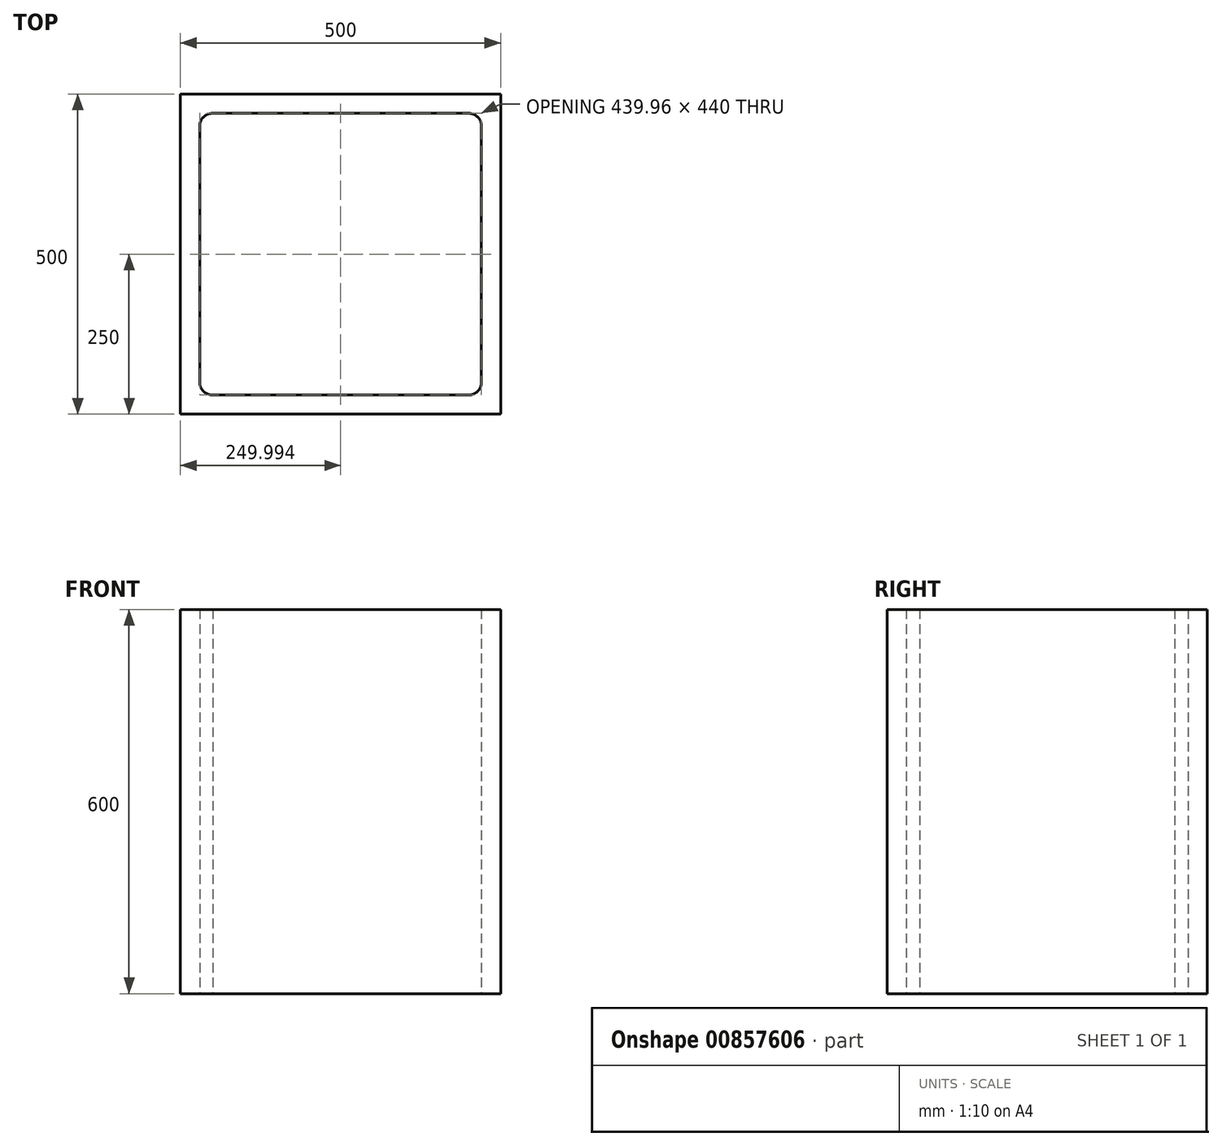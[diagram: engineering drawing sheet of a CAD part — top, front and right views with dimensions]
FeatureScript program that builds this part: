
annotation { "Feature Type Name" : "Feature", "Feature Type Description" : "" }
export const myFeature = defineFeature(function(context is Context, id is Id, definition is map)
    precondition{}
    {
        {
            var Q0;
            Q0=qCreatedBy(makeId("Top.planeOp"),FACE);
            var sketch = newSketch(context, id + "F0", { "sketchPlane" : qUnion([Q0])});
            skLineSegment(sketch, "E0.bottom", {"start": v(250, 250) * mm, "end": v(-250, 250) * mm});
            skLineSegment(sketch, "E0.top", {"start": v(250, -250) * mm, "end": v(-250, -250) * mm});
            skLineSegment(sketch, "E0.left", {"start": v(250, 250) * mm, "end": v(250, -250) * mm});
            skLineSegment(sketch, "E0.right", {"start": v(-250, 250) * mm, "end": v(-250, -250) * mm});
            skPoint(sketch, "E0.middle", {"position": v(0, 0) * mm});
            skLineSegment(sketch, "E1.bottom", {"start": v(200, 200) * mm, "end": v(-200, 200) * mm, "construction": true});
            skLineSegment(sketch, "E1.top", {"start": v(200, -200) * mm, "end": v(-200, -200) * mm, "construction": true});
            skLineSegment(sketch, "E1.left", {"start": v(200, 200) * mm, "end": v(200, -200) * mm, "construction": true});
            skLineSegment(sketch, "E1.right", {"start": v(-200, 200) * mm, "end": v(-200, -200) * mm, "construction": true});
            skArc(sketch, "E2", {"start": v(-199.85, 220) * mm, "mid": v(-214.34, 213.94) * mm, "end": v(-219.99, 199.3) * mm});
            skArc(sketch, "E3", {"start": v(219.98, 199.03) * mm, "mid": v(214.48, 213.8) * mm, "end": v(200, 220) * mm});
            skArc(sketch, "E4", {"start": v(200, -220) * mm, "mid": v(214.48, -213.8) * mm, "end": v(219.98, -199.03) * mm});
            skArc(sketch, "E5", {"start": v(-219.99, -199.3) * mm, "mid": v(-214.27, -214) * mm, "end": v(-199.67, -220) * mm});
            skLineSegment(sketch, "E6", {"start": v(-200.15, 220) * mm, "end": v(200, 220) * mm});
            skLineSegment(sketch, "E7", {"start": v(-219.99, 200.7) * mm, "end": v(-219.99, -200.7) * mm});
            skLineSegment(sketch, "E8", {"start": v(-200.33, -220) * mm, "end": v(200, -220) * mm});
            skLineSegment(sketch, "E9", {"start": v(219.98, -199.03) * mm, "end": v(219.98, 200) * mm});
            skSolve(sketch);
        }
        {
            var Q0;
            Q0 = qSketchRegion(id + "F0", true);
            extrude(context, id + "F1", {"entities" : qUnion([Q0]), "depth" : 600 * mm, "offsetDistance" : 25 * mm});
        }
    });
